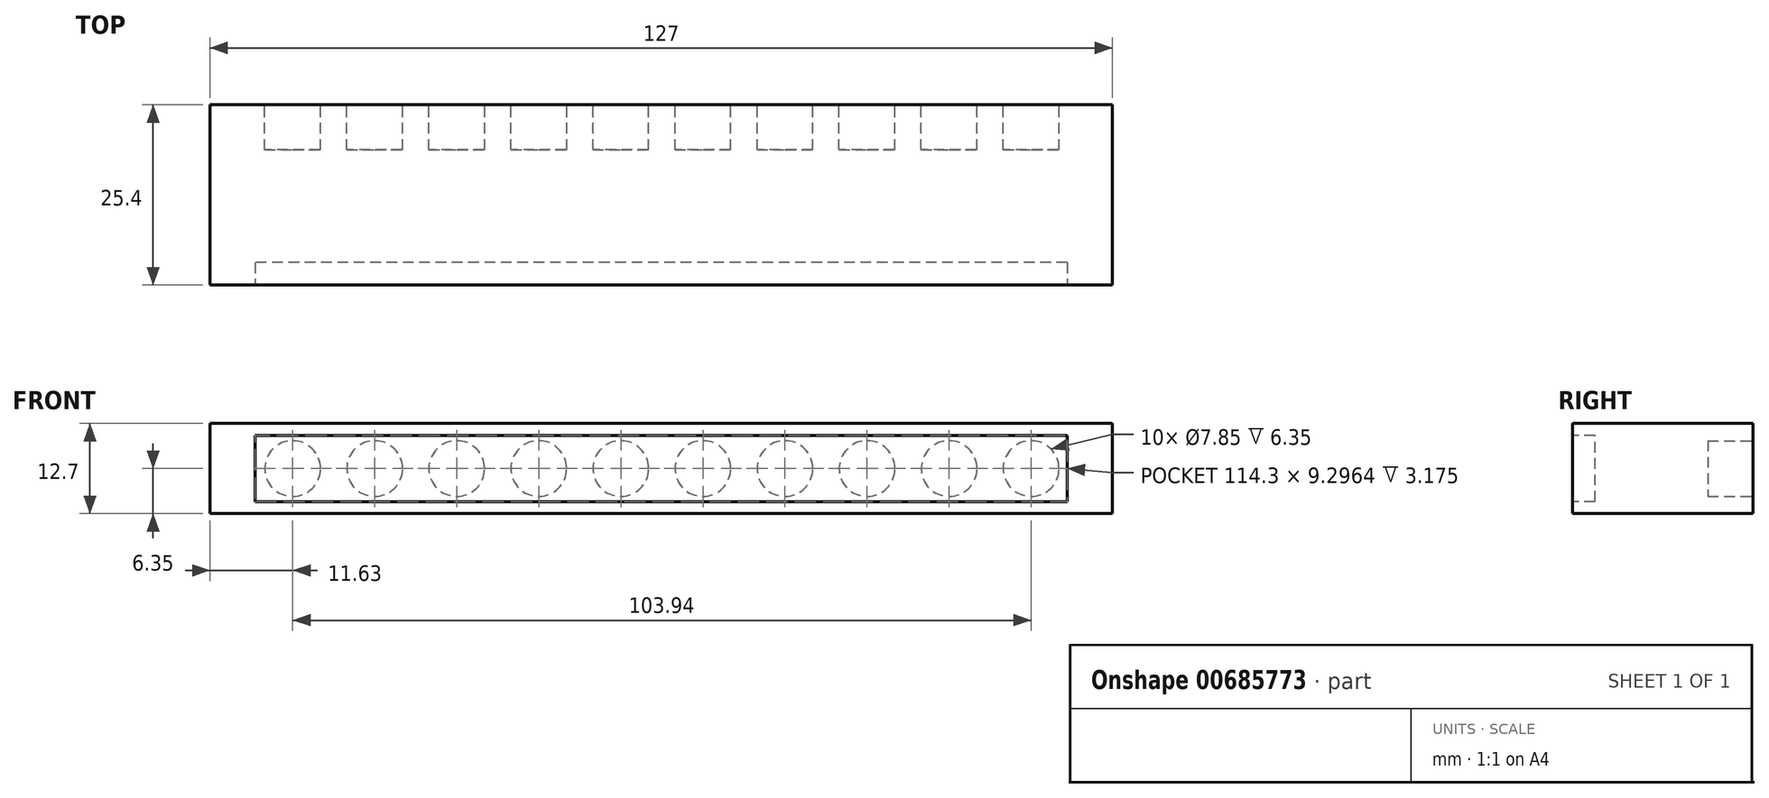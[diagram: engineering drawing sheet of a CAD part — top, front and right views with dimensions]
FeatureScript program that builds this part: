
annotation { "Feature Type Name" : "Feature", "Feature Type Description" : "" }
export const myFeature = defineFeature(function(context is Context, id is Id, definition is map)
    precondition{}
    {
        {
            var Q0;
            Q0=qCreatedBy(makeId("Front.planeOp"),FACE);
            var sketch = newSketch(context, id + "F0", { "sketchPlane" : qUnion([Q0])});
            skLineSegment(sketch, "E0.bottom", {"start": v(63.5, 6.35) * mm, "end": v(-63.5, 6.35) * mm});
            skLineSegment(sketch, "E0.top", {"start": v(63.5, -6.35) * mm, "end": v(-63.5, -6.35) * mm});
            skLineSegment(sketch, "E0.left", {"start": v(63.5, 6.35) * mm, "end": v(63.5, -6.35) * mm});
            skLineSegment(sketch, "E0.right", {"start": v(-63.5, 6.35) * mm, "end": v(-63.5, -6.35) * mm});
            skPoint(sketch, "E0.middle", {"position": v(0, 0) * mm});
            skSolve(sketch);
        }
        {
            var Q0;
            Q0=makeQuery(id+"F0.imprint","IMPRINT",FACE,{"disambiguationData":[TD([[makeQuery(id+"F0.imprint","IMPRINT",EDGE,{"derivedFrom":sQuery(id+"F0.wireOp",EDGE,"E0.bottom")}),1.0]])]});
            extrude(context, id + "F1", {"entities" : qUnion([Q0]), "depth" : 25.4 * mm, "offsetDistance" : 25.4 * mm});
        }
        {
            var Q0;
            Q0=makeQuery(id+"F1.opExtrude","CAP_FACE",FACE,{"disambiguationData":[OSD([sQuery(id+"F0.wireOp",EDGE,"E0.bottom"),sQuery(id+"F0.wireOp",EDGE,"E0.top"),sQuery(id+"F0.wireOp",EDGE,"E0.left"),sQuery(id+"F0.wireOp",EDGE,"E0.right")])],"isStart":true});
            var sketch = newSketch(context, id + "F2", { "sketchPlane" : qUnion([Q0])});
            skCircle(sketch, "E1", {"center": v(-52.07, 0) * mm, "radius": 3.92 * mm});
            skCircle(sketch, "E2.1.0.0", {"center": v(-40.52, 0) * mm, "radius": 3.92 * mm});
            skCircle(sketch, "E2.2.0.0", {"center": v(-28.97, 0) * mm, "radius": 3.92 * mm});
            skCircle(sketch, "E2.3.0.0", {"center": v(-17.42, 0) * mm, "radius": 3.92 * mm});
            skCircle(sketch, "E2.4.0.0", {"center": v(-5.87, 0) * mm, "radius": 3.92 * mm});
            skCircle(sketch, "E2.5.0.0", {"center": v(5.68, 0) * mm, "radius": 3.92 * mm});
            skCircle(sketch, "E2.6.0.0", {"center": v(17.22, 0) * mm, "radius": 3.92 * mm});
            skCircle(sketch, "E2.7.0.0", {"center": v(28.77, 0) * mm, "radius": 3.92 * mm});
            skCircle(sketch, "E2.8.0.0", {"center": v(40.32, 0) * mm, "radius": 3.92 * mm});
            skCircle(sketch, "E2.9.0.0", {"center": v(51.87, 0) * mm, "radius": 3.92 * mm});
            skLineSegment(sketch, "E2.direction1", {"start": v(-52.07, 0) * mm, "end": v(-40.52, 0) * mm, "construction": true});
            skSolve(sketch);
        }
        {
            var Q0;
            Q0=makeQuery(id+"F2.imprint","IMPRINT",FACE,{"disambiguationData":[TD([[makeQuery(id+"F2.imprint","IMPRINT",EDGE,{"derivedFrom":sQuery(id+"F2.wireOp",EDGE,"E2.8.0.0")}),1.0]])]});
            var Q1;
            Q1 = qSketchRegion(id + "F2", true);
            extrude(context, id + "F3", {"entities" : qUnion([Q0, Q1]), "operationType" : NewBodyOperationType.REMOVE, "oppositeDirection" : true, "depth" : 6.35 * mm, "offsetDistance" : 25.4 * mm});
        }
        {
            var Q0;
            Q0=makeQuery(id+"F1.opExtrude","CAP_FACE",FACE,{"disambiguationData":[OSD([sQuery(id+"F0.wireOp",EDGE,"E0.bottom"),sQuery(id+"F0.wireOp",EDGE,"E0.top"),sQuery(id+"F0.wireOp",EDGE,"E0.left"),sQuery(id+"F0.wireOp",EDGE,"E0.right")])],"isStart":false});
            var sketch = newSketch(context, id + "F4", { "sketchPlane" : qUnion([Q0])});
            skLineSegment(sketch, "E3.bottom", {"start": v(57.15, -4.65) * mm, "end": v(-57.15, -4.65) * mm});
            skLineSegment(sketch, "E3.top", {"start": v(57.15, 4.65) * mm, "end": v(-57.15, 4.65) * mm});
            skLineSegment(sketch, "E3.left", {"start": v(57.15, -4.65) * mm, "end": v(57.15, 4.65) * mm});
            skLineSegment(sketch, "E3.right", {"start": v(-57.15, -4.65) * mm, "end": v(-57.15, 4.65) * mm});
            skPoint(sketch, "E3.middle", {"position": v(0, 0) * mm});
            skSolve(sketch);
        }
        {
            var Q0;
            Q0=makeQuery(id+"F4.imprint","IMPRINT",FACE,{"disambiguationData":[TD([[makeQuery(id+"F4.imprint","IMPRINT",EDGE,{"derivedFrom":sQuery(id+"F4.wireOp",EDGE,"E3.bottom")}),-1.0]])]});
            extrude(context, id + "F5", {"entities" : qUnion([Q0]), "operationType" : NewBodyOperationType.REMOVE, "oppositeDirection" : true, "depth" : 3.17 * mm, "offsetDistance" : 25.4 * mm});
        }
    });
